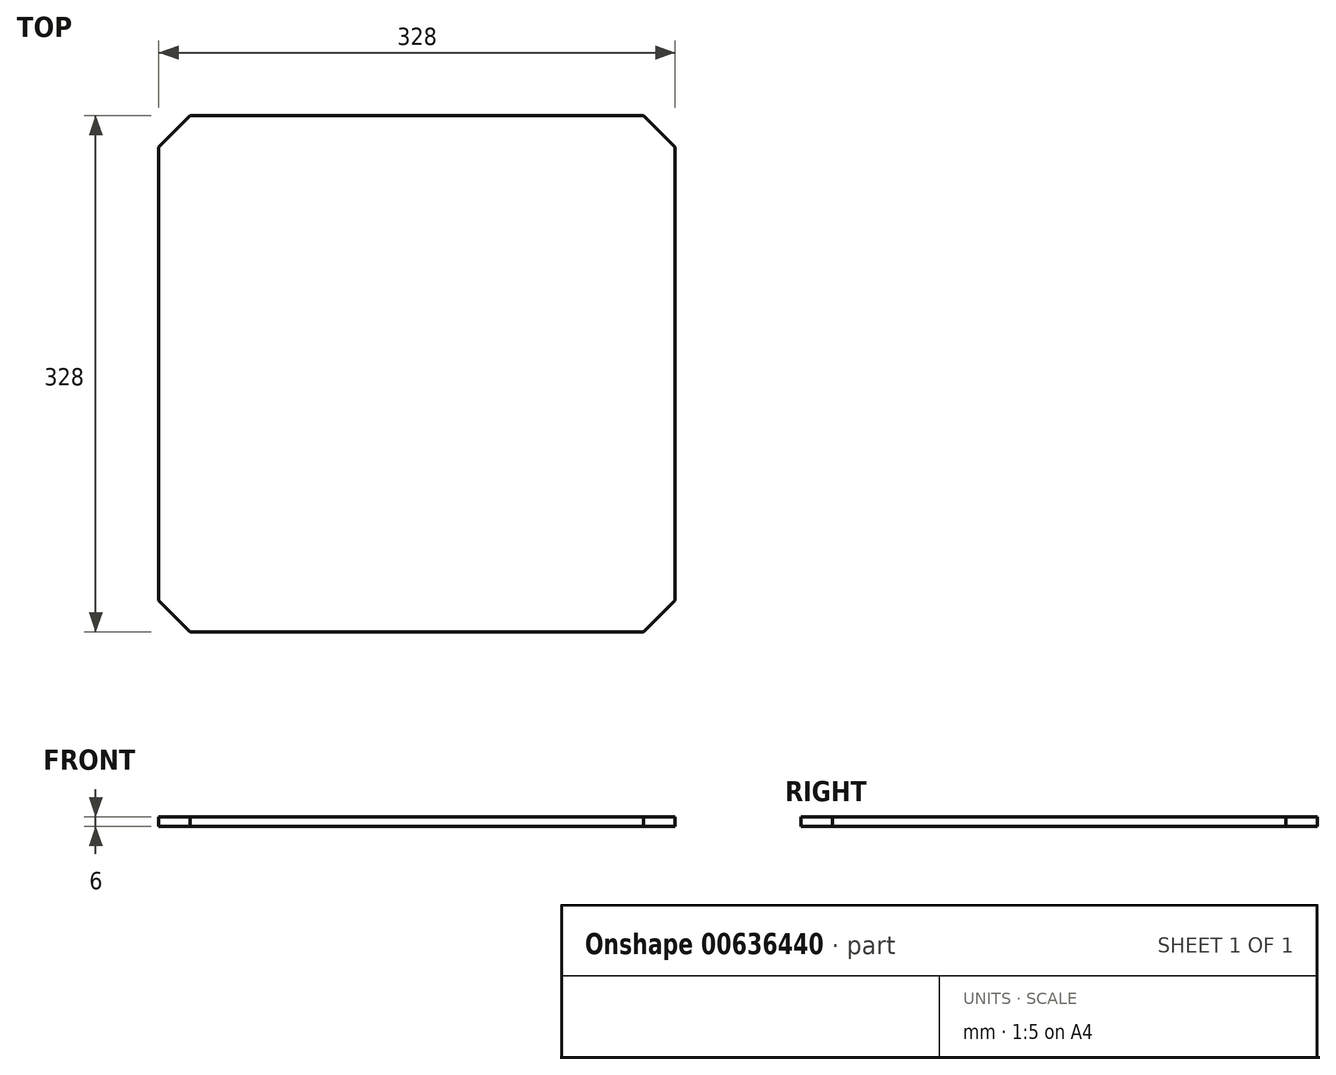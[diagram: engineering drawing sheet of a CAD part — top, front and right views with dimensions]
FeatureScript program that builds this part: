
annotation { "Feature Type Name" : "Feature", "Feature Type Description" : "" }
export const myFeature = defineFeature(function(context is Context, id is Id, definition is map)
    precondition{}
    {
        {
            var Q0;
            Q0=qCreatedBy(makeId("Top.planeOp"),FACE);
            var sketch = newSketch(context, id + "F0", { "sketchPlane" : qUnion([Q0])});
            skLineSegment(sketch, "E0.bottom", {"start": v(0, 0) * mm, "end": v(328, 0) * mm});
            skLineSegment(sketch, "E0.top", {"start": v(0, 328) * mm, "end": v(328, 328) * mm});
            skLineSegment(sketch, "E0.left", {"start": v(0, 0) * mm, "end": v(0, 328) * mm});
            skLineSegment(sketch, "E0.right", {"start": v(328, 0) * mm, "end": v(328, 328) * mm});
            skSolve(sketch);
        }
        {
            var Q0;
            Q0 = qSketchRegion(id + "F0", true);
            extrude(context, id + "F1", {"entities" : qUnion([Q0]), "depth" : 6 * mm, "offsetDistance" : 25 * mm});
        }
        {
            var Q0;
            Q0=makeQuery(id+"F1.opExtrude","SWEPT_EDGE",EDGE,{"disambiguationData":[OSD([sQuery(id+"F0.wireOp",EDGE,"E0.top"),sQuery(id+"F0.wireOp",EDGE,"E0.right")])]});
            var Q1;
            Q1=makeQuery(id+"F1.opExtrude","SWEPT_EDGE",EDGE,{"disambiguationData":[OSD([sQuery(id+"F0.wireOp",EDGE,"E0.top"),sQuery(id+"F0.wireOp",EDGE,"E0.left")])]});
            var Q2;
            Q2=makeQuery(id+"F1.opExtrude","SWEPT_EDGE",EDGE,{"disambiguationData":[OSD([sQuery(id+"F0.wireOp",EDGE,"E0.bottom"),sQuery(id+"F0.wireOp",EDGE,"E0.left")])]});
            var Q3;
            Q3=makeQuery(id+"F1.opExtrude","SWEPT_EDGE",EDGE,{"disambiguationData":[OSD([sQuery(id+"F0.wireOp",EDGE,"E0.bottom"),sQuery(id+"F0.wireOp",EDGE,"E0.right")])]});
            chamfer(context, id + "F2", {"entities" : qUnion([Q0, Q1, Q2, Q3]), "width" : 20 * mm, "tangentPropagation" : true});
        }
    });
